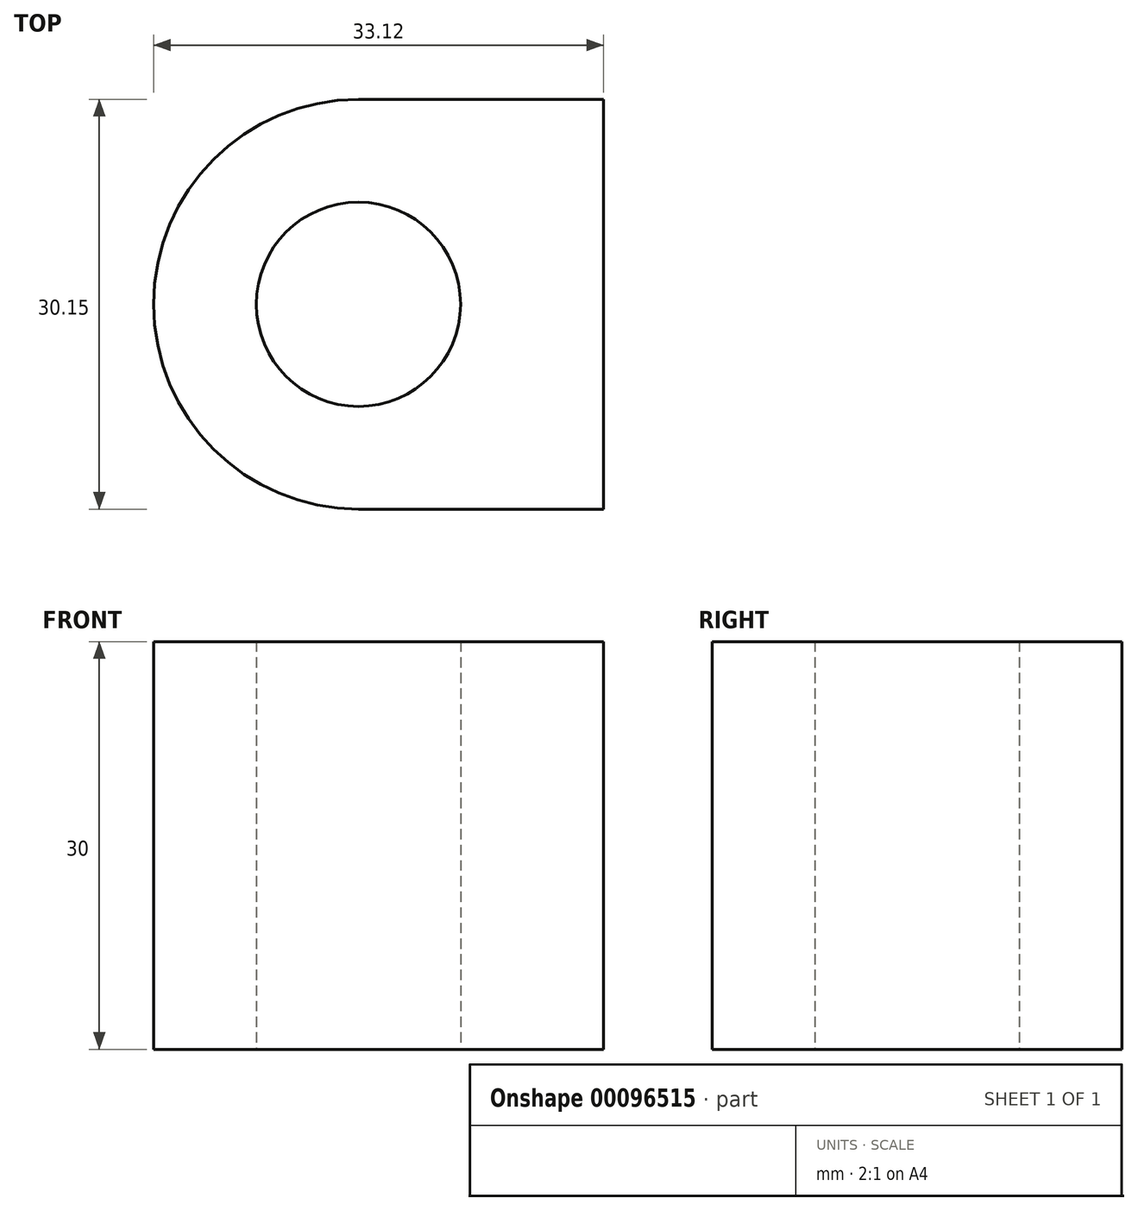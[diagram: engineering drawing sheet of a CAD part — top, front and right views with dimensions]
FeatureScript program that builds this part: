
annotation { "Feature Type Name" : "Feature", "Feature Type Description" : "" }
export const myFeature = defineFeature(function(context is Context, id is Id, definition is map)
    precondition{}
    {
        {
            var Q0;
            Q0=qCreatedBy(makeId("Top.planeOp"),FACE);
            var sketch = newSketch(context, id + "F0", { "sketchPlane" : qUnion([Q0])});
            skLineSegment(sketch, "E0.bottom", {"start": v(0, 0) * mm, "end": v(33.16, 0) * mm});
            skLineSegment(sketch, "E0.top", {"start": v(0, 30.15) * mm, "end": v(33.16, 30.15) * mm});
            skLineSegment(sketch, "E1", {"start": v(42.26, 20.89) * mm, "end": v(42.26, 8.86) * mm});
            skLineSegment(sketch, "E2", {"start": v(42.26, 8.86) * mm, "end": v(33.16, 0) * mm});
            skLineSegment(sketch, "E3", {"start": v(33.16, 30.15) * mm, "end": v(42.26, 20.89) * mm});
            skLineSegment(sketch, "E4", {"start": v(0, 30.15) * mm, "end": v(-18.04, 30.15) * mm});
            skLineSegment(sketch, "E5", {"start": v(-18.04, 0) * mm, "end": v(0, 0) * mm});
            skArc(sketch, "E6", {"start": v(-18.04, 30.15) * mm, "mid": v(-33.12, 15.08) * mm, "end": v(-18.04, 0) * mm});
            skCircle(sketch, "E7", {"center": v(-18.04, 15.08) * mm, "radius": 7.52 * mm});
            skPoint(sketch, "E8.endSnap0", {"position": v(42.26, 14.87) * mm});
            skLineSegment(sketch, "E9", {"start": v(0, 18.77) * mm, "end": v(42.26, 18.77) * mm});
            skLineSegment(sketch, "E10", {"start": v(0, 11.46) * mm, "end": v(42.26, 11.46) * mm});
            skLineSegment(sketch, "E11", {"start": v(0, 30.15) * mm, "end": v(0, 0) * mm});
            skSolve(sketch);
        }
        {
            var Q0;
            {var subQ1=sQuery(id+"F0.wireOp",EDGE,"E4");Q0=makeQuery(id+"F0.imprint","IMPRINT",FACE,{"disambiguationData":[TD([[makeQuery(id+"F0.imprint","IMPRINT",EDGE,{"derivedFrom":subQ1}),1.0]])]});}
            extrude(context, id + "F1", {"entities" : qUnion([Q0]), "depth" : 30 * mm});
        }
    });
